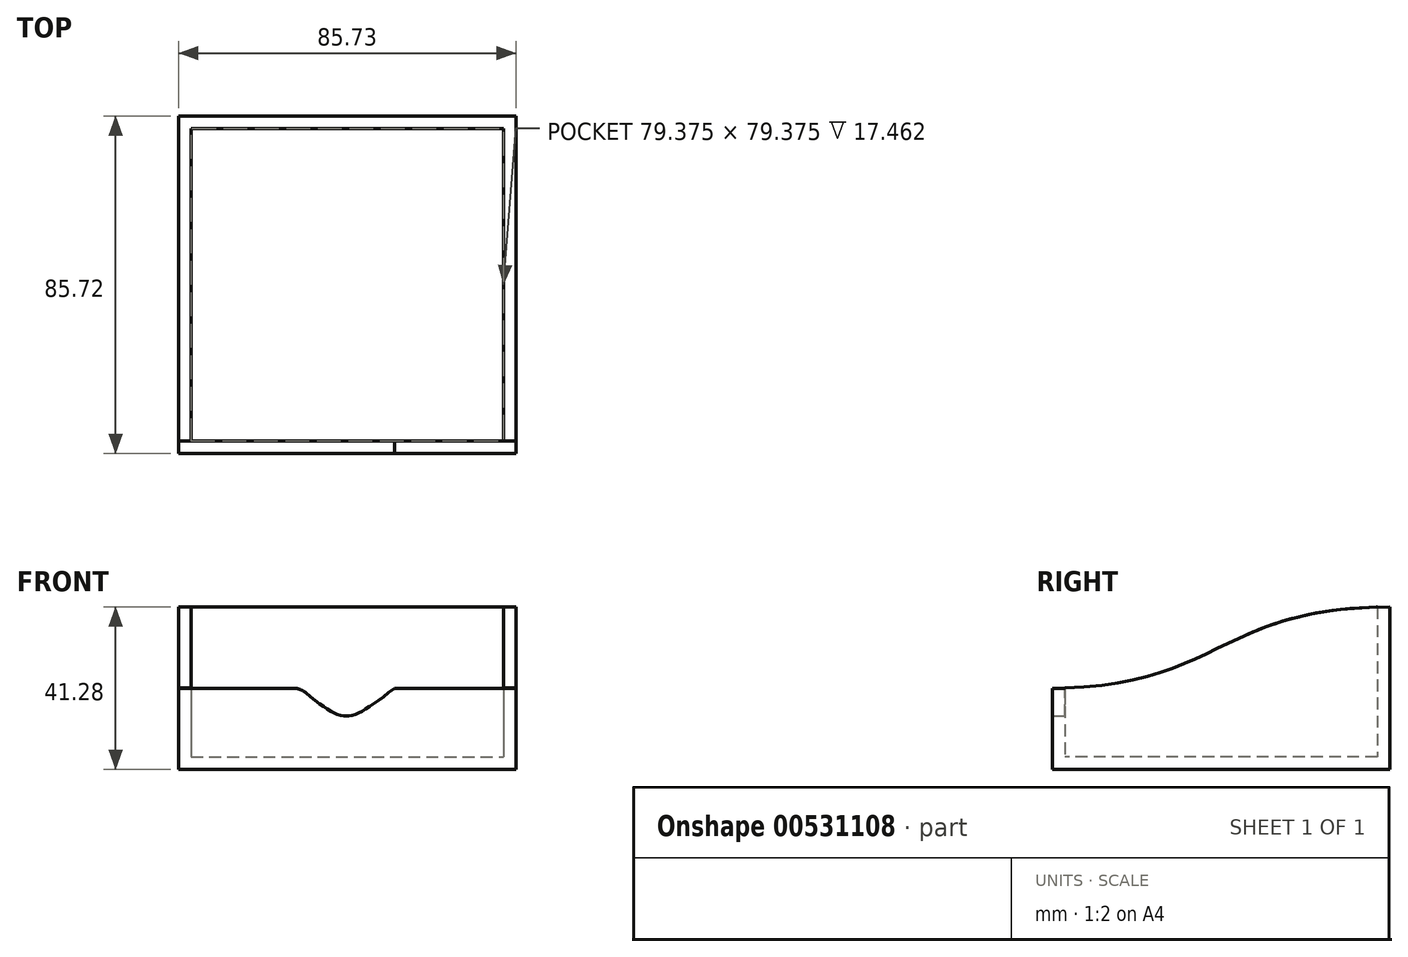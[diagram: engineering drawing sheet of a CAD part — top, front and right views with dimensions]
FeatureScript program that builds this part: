
annotation { "Feature Type Name" : "Feature", "Feature Type Description" : "" }
export const myFeature = defineFeature(function(context is Context, id is Id, definition is map)
    precondition{}
    {
        {
            var Q0;
            Q0=qCreatedBy(makeId("Top.planeOp"),FACE);
            var sketch = newSketch(context, id + "F0", { "sketchPlane" : qUnion([Q0])});
            skLineSegment(sketch, "E0.bottom", {"start": v(-39.37, 40.28) * mm, "end": v(40, 40.28) * mm});
            skLineSegment(sketch, "E0.top", {"start": v(-39.37, -39.1) * mm, "end": v(40, -39.1) * mm});
            skLineSegment(sketch, "E0.left", {"start": v(-39.37, 40.28) * mm, "end": v(-39.37, -39.1) * mm});
            skLineSegment(sketch, "E0.right", {"start": v(40, 40.28) * mm, "end": v(40, -39.1) * mm});
            skSolve(sketch);
        }
        {
            var Q0;
            Q0=makeQuery(id+"F0.imprint","IMPRINT",FACE,{"disambiguationData":[TD([[makeQuery(id+"F0.imprint","IMPRINT",EDGE,{"derivedFrom":sQuery(id+"F0.wireOp",EDGE,"E0.bottom")}),-1.0]])]});
            extrude(context, id + "F1", {"entities" : qUnion([Q0]), "depth" : 38.1 * mm, "offsetDistance" : 25.4 * mm});
        }
        {
            var Q0;
            Q0=makeQuery(id+"F1.opExtrude","CAP_FACE",FACE,{"disambiguationData":[OSD([sQuery(id+"F0.wireOp",EDGE,"E0.bottom"),sQuery(id+"F0.wireOp",EDGE,"E0.top"),sQuery(id+"F0.wireOp",EDGE,"E0.left"),sQuery(id+"F0.wireOp",EDGE,"E0.right")])],"isStart":false});
            shell(context, id + "F2", {"entities" : qUnion([Q0]), "thickness" : 3.17 * mm, "oppositeDirection" : true});
        }
        {
            var Q0;
            Q0=makeQuery(id+"F1.opExtrude","SWEPT_FACE",FACE,{"disambiguationData":[OSD([sQuery(id+"F0.wireOp",EDGE,"E0.right")])]});
            var sketch = newSketch(context, id + "F3", { "sketchPlane" : qUnion([Q0])});
            skFitSpline(sketch, "E1", {"points": [v(-42.27, 17.46) * mm, v(43.45, 38.1) * mm], "startDerivative": vector(126.81, 0) * mm, "endDerivative": vector(130.36, 0) * mm});
            skPoint(sketch, "E2", {"position": v(0.6, 38.1) * mm});
            skSolve(sketch);
        }
        {
            var Q0;
            {var subQ0=sQuery(id+"F3.wireOp",EDGE,"E1");Q0=makeQuery(id+"F3.imprint","IMPRINT",FACE,{"disambiguationData":[TD([[makeQuery(id+"F3.imprint","IMPRINT",EDGE,{"derivedFrom":subQ0}),1.0]])]});}
            extrude(context, id + "F4", {"entities" : qUnion([Q0]), "operationType" : NewBodyOperationType.REMOVE, "oppositeDirection" : true, "depth" : 85.72 * mm, "offsetDistance" : 25.4 * mm});
        }
        {
            var Q0;
            Q0=makeQuery(id+"F1.opExtrude","SWEPT_FACE",FACE,{"disambiguationData":[OSD([sQuery(id+"F0.wireOp",EDGE,"E0.top")])]});
            var sketch = newSketch(context, id + "F5", { "sketchPlane" : qUnion([Q0])});
            skFitSpline(sketch, "E3", {"points": [v(-11.68, 17.46) * mm, v(12.32, 17.46) * mm], "startDerivative": vector(35.02, -28.45) * mm, "endDerivative": vector(36.96, 28.21) * mm});
            skLineSegment(sketch, "E4.bottom", {"start": v(-11.68, 17.46) * mm, "end": v(12.32, 17.46) * mm});
            skSolve(sketch);
        }
        {
            var Q0;
            {var subQ0=sQuery(id+"F5.wireOp",EDGE,"E3");Q0=makeQuery(id+"F5.imprint","IMPRINT",FACE,{"disambiguationData":[TD([[makeQuery(id+"F5.imprint","IMPRINT",EDGE,{"derivedFrom":subQ0}),1.0]])]});}
            var Q1;
            Q1=makeQuery(id+"F5.imprint","IMPRINT",FACE,{"disambiguationData":[TD([[makeQuery(id+"F5.imprint","IMPRINT",EDGE,{"derivedFrom":sQuery(id+"F5.wireOp",EDGE,"E4.bottom")}),1.0]])]});
            extrude(context, id + "F6", {"entities" : qUnion([Q0, Q1]), "operationType" : NewBodyOperationType.REMOVE, "oppositeDirection" : true, "depth" : 3.17 * mm, "offsetDistance" : 25.4 * mm});
        }
        {
            var Q0;
            Q0=makeQuery(id+"F1.opExtrude","SWEPT_FACE",FACE,{"disambiguationData":[OSD([sQuery(id+"F0.wireOp",EDGE,"E0.top")])]});
            var sketch = newSketch(context, id + "F7", { "sketchPlane" : qUnion([Q0])});
            skLineSegment(sketch, "E5.bottom", {"start": v(-42.55, 17.46) * mm, "end": v(43.18, 17.46) * mm});
            skLineSegment(sketch, "E5.top", {"start": v(-42.55, 18.48) * mm, "end": v(43.18, 18.48) * mm});
            skLineSegment(sketch, "E5.left", {"start": v(-42.55, 17.46) * mm, "end": v(-42.55, 18.48) * mm});
            skLineSegment(sketch, "E5.right", {"start": v(43.18, 17.46) * mm, "end": v(43.18, 18.48) * mm});
            skSolve(sketch);
        }
        {
            var Q0;
            Q0=makeQuery(id+"F7.imprint","IMPRINT",FACE,{"disambiguationData":[TD([[makeQuery(id+"F7.imprint","IMPRINT",EDGE,{"derivedFrom":sQuery(id+"F7.wireOp",EDGE,"E5.top")}),-1.0]])]});
            extrude(context, id + "F8", {"entities" : qUnion([Q0]), "operationType" : NewBodyOperationType.REMOVE, "oppositeDirection" : true, "depth" : 3.17 * mm, "offsetDistance" : 25.4 * mm});
        }
        {
            var Q0;
            {var subQ0=sQuery(id+"F5.wireOp",EDGE,"E4.bottom");var subQ1=sQuery(id+"F5.wireOp",EDGE,"E3");var subQ2=sQuery(id+"F3.wireOp",EDGE,"E1");var subQ3=sQuery(id+"F0.wireOp",EDGE,"E0.right");var subQ4=sQuery(id+"F0.wireOp",EDGE,"E0.top");Q0=makeQuery(id+"F6.boolean.opBoolean","COPY",EDGE,{"derivedFrom":makeQuery(id+"F6.opExtrude","SWEPT_EDGE",EDGE,{"disambiguationData":[OSD([subQ4,subQ3,subQ2,subQ1,subQ0]),TDD([makeQuery(id+"F5.imprint","INTERSECT",VERTEX,{"disambiguationData":[OD(1.0)],"derivedFrom":[makeQuery(id+"F4.boolean.opBoolean","COPY",EDGE,{"derivedFrom":makeQuery(id+"F4.opExtrude","SWEPT_EDGE",EDGE,{"disambiguationData":[OSD([subQ4,subQ3,subQ2])]})}),subQ1,subQ0]})])]})});}
            var Q1;
            {var subQ0=sQuery(id+"F5.wireOp",EDGE,"E4.bottom");var subQ1=sQuery(id+"F5.wireOp",EDGE,"E3");var subQ2=sQuery(id+"F3.wireOp",EDGE,"E1");var subQ3=sQuery(id+"F0.wireOp",EDGE,"E0.right");var subQ4=sQuery(id+"F0.wireOp",EDGE,"E0.top");Q1=makeQuery(id+"F6.boolean.opBoolean","COPY",EDGE,{"derivedFrom":makeQuery(id+"F6.opExtrude","SWEPT_EDGE",EDGE,{"disambiguationData":[OSD([subQ4,subQ3,subQ2,subQ1,subQ0]),TDD([makeQuery(id+"F5.imprint","INTERSECT",VERTEX,{"disambiguationData":[OD(0.0)],"derivedFrom":[makeQuery(id+"F4.boolean.opBoolean","COPY",EDGE,{"derivedFrom":makeQuery(id+"F4.opExtrude","SWEPT_EDGE",EDGE,{"disambiguationData":[OSD([subQ4,subQ3,subQ2])]})}),subQ1,subQ0]})])]})});}
            fillet(context, id + "F9", {"entities" : qUnion([Q0, Q1]), "radius" : 5.08 * mm, "tangentPropagation" : true, "allowEdgeOverflow" : false});
        }
    });
